# Revit family: IMH_ARR_10
name_source: partatom
category: Mechanical Equipment
units: mm (PartAtom-declared; Revit-internal decimal feet)

## family parameters
Always vertical = No
Cut with Voids When Loaded = No
Part Type = Normal
Room Calculation Point = No
Round Connector Dimension = Use Radius
Shared = No
Work Plane-Based = No

## types (44) — shared parameters
0 = 0"
1" = 1"
1.5 = 1 1/2"
2" = 2"
2' = 24"
3" = 3"
4" = 4"
90 = 90.00°
BAD = No
BAD_CCW = No
BAD_CW = No
BAU = No
BAU_CCW = No
BAU_CW = No
BHD = No
BHD_CCW = No
BHD_CW = No
CCW = No
CW = Yes
DBD = No
DBD_CCW = No
DBD_CW = No
FIRST_CURVE = 0"
L_RAD = 18 5/32"
Manufacturer = Loren Cook Company
NO = No
ONE EIGTH = 1/8"
TAD = No
TAD_CCW = No
TAD_CW = No
TAU = No
TAU_CCW = No
TAU_CW = No
THD = Yes
THD_CCW = No
THD_CW = Yes
UBD = No
UBD_CCW = No
UBD_CW = No
URL = www.lorencook.com
ZERO = 0.00°

## per-type parameters (varying)
- 70_MHA_ARR_10: (B + 1/4") / 2=3 1/16"; (C/2)+2"=5 1/2"; (C/2)-.125"=3 3/8"; (N-A)/2=1 31/32"; -((B + 1/4") / 2)=-3 1/16"; -D=-14 1/4"; -D+.125"=-14 1/8"; -F=-21 1/16"; -R*.75=-11 5/32"; 2S=8 1/2"; 2T=2 3/8"; 91*AA=8 1/32"; A=6 5/8"; A+.25"=6 7/8"; A/2=3 5/16"; A/5=1 5/16"; AA=8 13/16"; B=5 7/8"; B+.25"=6 1/8"; B/2=2 15/16"; BB=8 3/8"; C=7"; C/2=3 1/2"; D=14 1/4"; E=9 11/16"; E-2"=7 11/16"; E/2=4 27/32"; F=21 1/16"; G=26 1/4"; H=24 3/16"; J=4"; K=9 3/16"; L=9 11/16"; M=8 5/16"; M*.9=7"; M-(A/5)=7"; M/2=4 5/32"; Model=MHA; N=10 9/16"; N-A=3 15/16"; P=9/16"; P/2=9/32"; Q=7 7/16"; R=14 7/8"; R*.75=-11 5/32"; S=4 1/4"; SECOND_CURVE=27/32"; T=1 3/16"; T+T+1"=3 3/8"; T/2=19/32"; THIRD_CURVE=1 3/32"; Type Comments=Industrial Material Handler Backward Inclined Flat Blade Belt Driven Single Width, Single Inlet Arrangement 10; U=6 3/16"; UNIT_SIZE=70; W=6"; X=10 1/8"; Y=9 1/4"; Z=13 3/8"
- 90_MHA_ARR_10: (B + 1/4") / 2=3 7/8"; (C/2)+2"=6 1/2"; (C/2)-.125"=4 3/8"; (N-A)/2=2 17/32"; -((B + 1/4") / 2)=-3 7/8"; -D=-15 1/4"; -D+.125"=-15 1/8"; -F=-21 7/8"; -R*.75=-11 5/32"; 2S=10 1/8"; 2T=2 7/8"; 91*AA=10 3/16"; A=8 7/16"; A+.25"=8 11/16"; A/2=4 7/32"; A/5=1 11/16"; AA=11 3/16"; B=7 1/2"; B+.25"=7 3/4"; B/2=3 3/4"; BB=10 5/8"; C=9"; C/2=4 1/2"; D=15 1/4"; E=9 11/16"; E-2"=7 11/16"; E/2=4 27/32"; F=21 7/8"; G=27 7/8"; H=28 3/4"; J=4"; K=9 3/16"; L=12 5/16"; M=10 5/8"; M*.9=8 15/16"; M-(A/5)=8 15/16"; M/2=5 5/16"; Model=MHA; N=13 1/2"; N-A=5 1/16"; P=9/16"; P/2=9/32"; Q=7 7/16"; R=14 7/8"; R*.75=-11 5/32"; S=5 1/16"; SECOND_CURVE=1 1/16"; T=1 7/16"; T+T+1"=3 7/8"; T/2=23/32"; THIRD_CURVE=1 13/32"; Type Comments=Industrial Material Handler Backward Inclined Flat Blade Belt Driven Single Width, Single Inlet Arrangement 10; U=7"; UNIT_SIZE=90; W=6"; X=12 15/16"; Y=11 3/4"; Z=17 1/16"
- 110_MHA_ARR_10: (B + 1/4") / 2=4 11/16"; (C/2)+2"=7 1/2"; (C/2)-.125"=5 3/8"; (N-A)/2=3 1/32"; -((B + 1/4") / 2)=-4 11/16"; -D=-18 3/4"; -D+.125"=-18 5/8"; -F=-25"; -R*.75=-12 3/8"; 2S=13"; 2T=2 7/8"; 91*AA=12 1/2"; A=10 3/8"; A+.25"=10 5/8"; A/2=5 3/16"; A/5=2 1/16"; AA=13 3/4"; B=9 1/8"; B+.25"=9 3/8"; B/2=4 9/16"; BB=13 1/16"; C=11"; C/2=5 1/2"; D=18 3/4"; E=9 11/16"; E-2"=7 11/16"; E/2=4 27/32"; F=25"; G=32 7/8"; H=35 3/16"; J=4"; K=9 3/16"; L=15 1/16"; M=13"; M*.9=10 15/16"; M-(A/5)=10 15/16"; M/2=6 1/2"; Model=MHA; N=16 7/16"; N-A=6 1/16"; P=9/16"; P/2=9/32"; Q=8 1/4"; R=16 1/2"; R*.75=-12 3/8"; S=6 1/2"; SECOND_CURVE=1 5/16"; T=1 7/16"; T+T+1"=3 7/8"; T/2=23/32"; THIRD_CURVE=1 23/32"; Type Comments=Industrial Material Handler Backward Inclined Flat Blade Belt Driven Single Width, Single Inlet Arrangement 10; U=8 13/16"; UNIT_SIZE=110; W=8"; X=15 3/4"; Y=14 7/16"; Z=20 13/16"
- 130_MHA_ARR_10: (B + 1/4") / 2=5 9/16"; (C/2)+2"=8 1/2"; (C/2)-.125"=6 3/8"; (N-A)/2=3 5/8"; -((B + 1/4") / 2)=-5 9/16"; -D=-21 3/4"; -D+.125"=-21 5/8"; -F=-26 3/16"; -R*.75=-12 9/16"; 2S=14 3/4"; 2T=3 3/8"; 91*AA=14 23/32"; A=12 3/16"; A+.25"=12 7/16"; A/2=6 3/32"; A/5=2 7/16"; AA=16 3/16"; B=10 7/8"; B+.25"=11 1/8"; B/2=5 7/16"; BB=15 3/8"; C=13"; C/2=6 1/2"; D=21 3/4"; E=11 3/4"; E-2"=9 3/4"; E/2=5 7/8"; F=26 3/16"; G=34 7/8"; H=41 3/16"; J=5"; K=11"; L=17 13/16"; M=15 3/8"; M*.9=12 15/16"; M-(A/5)=12 15/16"; M/2=7 11/16"; Model=MHA; N=19 7/16"; N-A=7 1/4"; P=11/16"; P/2=11/32"; Q=8 3/8"; R=16 3/4"; R*.75=-12 9/16"; S=7 3/8"; SECOND_CURVE=1 17/32"; T=1 11/16"; T+T+1"=4 3/8"; T/2=27/32"; THIRD_CURVE=2 1/32"; Type Comments=Industrial Material Handler Backward Inclined Flat Blade Belt Driven Single Width, Single Inlet Arrangement 10; U=9 13/16"; UNIT_SIZE=130; W=8"; X=18 5/8"; Y=17"; Z=24 5/8"
- 150_MHA_ARR_10: (B + 1/4") / 2=6 13/32"; (C/2)+2"=9 1/2"; (C/2)-.125"=7 3/8"; (N-A)/2=4 5/32"; -((B + 1/4") / 2)=-6 13/32"; -D=-25 1/4"; -D+.125"=-25 1/8"; -F=-31 3/4"; -R*.75=-16 1/8"; 2S=16 7/16"; 2T=3 7/8"; 91*AA=17 3/16"; A=14 1/16"; A+.25"=14 5/16"; A/2=7 1/32"; A/5=2 13/16"; AA=18 7/8"; B=12 9/16"; B+.25"=12 13/16"; B/2=6 9/32"; BB=18"; C=15"; C/2=7 1/2"; D=25 1/4"; E=13"; E-2"=11"; E/2=6 1/2"; F=31 3/4"; G=41 5/16"; H=47 5/8"; J=5"; K=12 1/4"; L=20 5/8"; M=17 3/4"; M*.9=14 15/16"; M-(A/5)=14 15/16"; M/2=8 7/8"; Model=MHA; N=22 3/8"; N-A=8 5/16"; P=11/16"; P/2=11/32"; Q=10 3/4"; R=21 1/2"; R*.75=-16 1/8"; S=8 7/32"; SECOND_CURVE=1 3/4"; T=1 15/16"; T+T+1"=4 7/8"; T/2=31/32"; THIRD_CURVE=2 11/32"; Type Comments=Industrial Material Handler Backward Inclined Flat Blade Belt Driven Single Width, Single Inlet Arrangement 10; U=10 11/16"; UNIT_SIZE=150; W=8"; X=21 1/2"; Y=19 3/4"; Z=28 3/8"
- 170_MHA_ARR_10: (B + 1/4") / 2=7 1/4"; (C/2)+2"=10 1/2"; (C/2)-.125"=8 3/8"; (N-A)/2=4 11/16"; -((B + 1/4") / 2)=-7 1/4"; -D=-28 1/4"; -D+.125"=-28 1/8"; -F=-32 9/16"; -R*.75=-16 1/8"; 2S=18 1/8"; 2T=4 3/8"; 91*AA=19 11/32"; A=16"; A+.25"=16 1/4"; A/2=8"; A/5=3 3/16"; AA=21 1/4"; B=14 1/4"; B+.25"=14 1/2"; B/2=7 1/8"; BB=20 1/4"; C=17"; C/2=8 1/2"; D=28 1/4"; E=13 7/8"; E-2"=11 7/8"; E/2=6 15/16"; F=32 9/16"; G=43"; H=53 5/8"; J=6"; K=13 1/8"; L=23 3/4"; M=20 1/8"; M*.9=16 15/16"; M-(A/5)=16 15/16"; M/2=10 1/16"; Model=MHA; N=25 3/8"; N-A=9 3/8"; P=11/16"; P/2=11/32"; Q=10 3/4"; R=21 1/2"; R*.75=-16 1/8"; S=9 1/16"; SECOND_CURVE=2"; T=2 3/16"; T+T+1"=5 3/8"; T/2=1 3/32"; THIRD_CURVE=2 21/32"; Type Comments=Industrial Material Handler Backward Inclined Flat Blade Belt Driven Single Width, Single Inlet Arrangement 10; U=11 1/2"; UNIT_SIZE=170; W=8"; X=24 9/16"; Y=22 1/2"; Z=32 3/16"
- 190_MHA_ARR_10: (B + 1/4") / 2=8 1/16"; (C/2)+2"=11 1/2"; (C/2)-.125"=9 3/8"; (N-A)/2=5 7/32"; -((B + 1/4") / 2)=-8 1/16"; -D=-31 1/4"; -D+.125"=-31 1/8"; -F=-34 11/16"; -R*.75=-17 1/16"; 2S=19 7/8"; 2T=4 7/8"; 91*AA=21 5/8"; A=17 13/16"; A+.25"=18 1/16"; A/2=8 29/32"; A/5=3 9/16"; AA=23 3/4"; B=15 7/8"; B+.25"=16 1/8"; B/2=7 15/16"; BB=22 5/8"; C=19"; C/2=9 1/2"; D=31 1/4"; E=15 5/16"; E-2"=13 5/16"; E/2=7 21/32"; F=34 11/16"; G=46"; H=59 1/2"; J=6"; K=14 9/16"; L=25 15/16"; M=22 7/16"; M*.9=18 7/8"; M-(A/5)=18 7/8"; M/2=11 7/32"; Model=MHA; N=28 1/4"; N-A=10 7/16"; P=11/16"; P/2=11/32"; Q=11 3/8"; R=22 3/4"; R*.75=-17 1/16"; S=9 15/16"; SECOND_CURVE=2 7/32"; T=2 7/16"; T+T+1"=5 7/8"; T/2=1 7/32"; THIRD_CURVE=2 31/32"; Type Comments=Industrial Material Handler Backward Inclined Flat Blade Belt Driven Single Width, Single Inlet Arrangement 10; U=12 5/16"; UNIT_SIZE=190; W=8"; X=27 1/8"; Y=24 7/8"; Z=35 13/16"
- 210_MHA_ARR_10: (B + 1/4") / 2=8 29/32"; (C/2)+2"=12 1/2"; (C/2)-.125"=10 3/8"; (N-A)/2=5 3/4"; -((B + 1/4") / 2)=-8 29/32"; -D=-34 1/2"; -D+.125"=-34 3/8"; -F=-38 1/4"; -R*.75=-19 1/8"; 2S=21 5/16"; 2T=4 7/8"; 91*AA=23 7/16"; A=19 3/4"; A+.25"=20"; A/2=9 7/8"; A/5=3 15/16"; AA=25 3/4"; B=17 9/16"; B+.25"=17 13/16"; B/2=8 25/32"; BB=24 3/8"; C=21"; C/2=10 1/2"; D=34 1/2"; E=16 9/16"; E-2"=14 9/16"; E/2=8 9/32"; F=38 1/4"; G=50 3/8"; H=65 3/4"; J=6"; K=15 13/16"; L=28 1/2"; M=23"; M*.9=19 1/16"; M-(A/5)=19 1/16"; M/2=11 1/2"; Model=MHA; N=31 1/4"; N-A=11 1/2"; P=11/16"; P/2=11/32"; Q=12 3/4"; R=25 1/2"; R*.75=-19 1/8"; S=10 21/32"; SECOND_CURVE=2 15/32"; T=2 7/16"; T+T+1"=5 7/8"; T/2=1 7/32"; THIRD_CURVE=3 9/32"; Type Comments=Industrial Material Handler Backward Inclined Flat Blade Belt Driven Single Width, Single Inlet Arrangement 10; U=13 3/16"; UNIT_SIZE=210; W=8"; X=29 7/8"; Y=27 1/8"; Z=38 3/8"
- 230_MHA_ARR_10: (B + 1/4") / 2=9 3/4"; (C/2)+2"=13 1/2"; (C/2)-.125"=11 3/8"; (N-A)/2=6 11/32"; -((B + 1/4") / 2)=-9 3/4"; -D=-37 1/2"; -D+.125"=-37 3/8"; -F=-41 1/8"; -R*.75=-20 5/32"; 2S=24 5/8"; 2T=5 3/8"; 91*AA=25 3/4"; A=21 5/8"; A+.25"=21 7/8"; A/2=10 13/16"; A/5=4 5/16"; AA=28 5/16"; B=19 1/4"; B+.25"=19 1/2"; B/2=9 5/8"; BB=26 13/16"; C=23"; C/2=11 1/2"; D=37 1/2"; E=18 13/16"; E-2"=16 13/16"; E/2=9 13/32"; F=41 1/8"; G=55 1/4"; H=71 13/16"; J=7"; K=17 9/16"; L=31 1/4"; M=26"; M*.9=21 11/16"; M-(A/5)=21 11/16"; M/2=13"; Model=MHA; N=34 5/16"; N-A=12 11/16"; P=13/16"; P/2=13/32"; Q=13 7/16"; R=26 7/8"; R*.75=-20 5/32"; S=12 5/16"; SECOND_CURVE=2 23/32"; T=2 11/16"; T+T+1"=6 3/8"; T/2=1 11/32"; THIRD_CURVE=3 19/32"; Type Comments=Industrial Material Handler Backward Inclined Flat Blade Belt Driven Single Width, Single Inlet Arrangement 10; U=15 1/8"; UNIT_SIZE=230; W=8"; X=32 13/16"; Y=29 13/16"; Z=42 5/8"
- 260_MHA_ARR_10: (B + 1/4") / 2=11"; (C/2)+2"=15"; (C/2)-.125"=12 7/8"; (N-A)/2=8 3/8"; -((B + 1/4") / 2)=-11"; -D=-41 3/4"; -D+.125"=-41 5/8"; -F=-43 15/16"; -R*.75=-20 13/16"; 2S=27 1/8"; 2T=5 3/8"; 91*AA=29"; A=24 7/16"; A+.25"=24 11/16"; A/2=12 7/32"; A/5=4 7/8"; AA=31 7/8"; B=21 3/4"; B+.25"=22"; B/2=10 7/8"; BB=30 1/4"; C=26"; C/2=13"; D=41 3/4"; E=20 5/8"; E-2"=18 5/8"; E/2=10 5/16"; F=43 15/16"; G=58 11/16"; H=82 15/16"; J=7"; K=19 3/8"; L=35 1/8"; M=29"; M*.9=24 1/8"; M-(A/5)=24 1/8"; M/2=14 1/2"; Model=MHA; N=41 3/16"; N-A=16 3/4"; P=13/16"; P/2=13/32"; Q=13 7/8"; R=27 3/4"; R*.75=-20 13/16"; S=13 9/16"; SECOND_CURVE=3 1/16"; T=2 11/16"; T+T+1"=6 3/8"; T/2=1 11/32"; THIRD_CURVE=4 1/16"; Type Comments=Industrial Material Handler Backward Inclined Flat Blade Belt Driven Single Width, Single Inlet Arrangement 10; U=16 3/8"; UNIT_SIZE=260; W=8"; X=38 3/16"; Y=33 1/2"; Z=49 5/8"
- 290_MHA_ARR_10: (B + 1/4") / 2=12 1/4"; (C/2)+2"=16 1/2"; (C/2)-.125"=14 3/8"; (N-A)/2=9 9/32"; -((B + 1/4") / 2)=-12 1/4"; -D=-46 1/2"; -D+.125"=-46 3/8"; -F=-45 9/16"; -R*.75=-21 9/16"; 2S=29 5/8"; 2T=5 7/8"; 91*AA=32 17/32"; A=27 5/16"; A+.25"=27 9/16"; A/2=13 21/32"; A/5=5 15/32"; AA=35 3/4"; B=24 1/4"; B+.25"=24 1/2"; B/2=12 1/8"; BB=33 7/8"; C=29"; C/2=14 1/2"; D=46 1/2"; E=22 1/2"; E-2"=20 1/2"; E/2=11 1/4"; F=45 9/16"; G=62 3/16"; H=92 1/2"; J=8"; K=21 1/4"; L=39 1/2"; M=31 3/4"; M*.9=26 9/32"; M-(A/5)=26 9/32"; M/2=15 7/8"; Model=MHA; N=45 7/8"; N-A=18 9/16"; P=13/16"; P/2=13/32"; Q=14 3/8"; R=28 3/4"; R*.75=-21 9/16"; S=14 13/16"; SECOND_CURVE=3 13/32"; T=2 15/16"; T+T+1"=6 7/8"; T/2=1 15/32"; THIRD_CURVE=4 9/16"; Type Comments=Industrial Material Handler Backward Inclined Flat Blade Belt Driven Single Width, Single Inlet Arrangement 10; U=17 5/8"; UNIT_SIZE=290; W=8"; X=42 11/16"; Y=37 5/8"; Z=54 7/8"
- 110_MHB_ARR_10: (B + 1/4") / 2=4 11/16"; (C/2)+2"=7 1/2"; (C/2)-.125"=5 3/8"; (N-A)/2=3 1/32"; -((B + 1/4") / 2)=-4 11/16"; -D=-18 3/4"; -D+.125"=-18 5/8"; -F=-25"; -R*.75=-12 3/8"; 2S=13"; 2T=2 7/8"; 91*AA=12 1/2"; A=10 3/8"; A+.25"=10 5/8"; A/2=5 3/16"; A/5=2 1/16"; AA=13 3/4"; B=9 1/8"; B+.25"=9 3/8"; B/2=4 9/16"; BB=13 1/16"; C=11"; C/2=5 1/2"; D=18 3/4"; E=9 11/16"; E-2"=7 11/16"; E/2=4 27/32"; F=25"; G=32 7/8"; H=35 3/16"; J=4"; K=9 3/16"; L=15 1/16"; M=13"; M*.9=10 15/16"; M-(A/5)=10 15/16"; M/2=6 1/2"; Model=MHB; N=16 7/16"; N-A=6 1/16"; P=9/16"; P/2=9/32"; Q=8 1/4"; R=16 1/2"; R*.75=-12 3/8"; S=6 1/2"; SECOND_CURVE=1 5/16"; T=1 7/16"; T+T+1"=3 7/8"; T/2=23/32"; THIRD_CURVE=1 23/32"; Type Comments=Industrial Material Handler Backward Inclined Backplated Radial Blade Belt Driven Single Width, Single Inlet Arrangement 10; U=8 13/16"; UNIT_SIZE=110; W=8"; X=15 3/4"; Y=14 7/16"; Z=20 13/16"
- 110_MHR_ARR_10: (B + 1/4") / 2=4 11/16"; (C/2)+2"=7 1/2"; (C/2)-.125"=5 3/8"; (N-A)/2=3 1/32"; -((B + 1/4") / 2)=-4 11/16"; -D=-18 3/4"; -D+.125"=-18 5/8"; -F=-25"; -R*.75=-12 3/8"; 2S=13"; 2T=2 7/8"; 91*AA=12 1/2"; A=10 3/8"; A+.25"=10 5/8"; A/2=5 3/16"; A/5=2 1/16"; AA=13 3/4"; B=9 1/8"; B+.25"=9 3/8"; B/2=4 9/16"; BB=13 1/16"; C=11"; C/2=5 1/2"; D=18 3/4"; E=9 11/16"; E-2"=7 11/16"; E/2=4 27/32"; F=25"; G=32 7/8"; H=35 3/16"; J=4"; K=9 3/16"; L=15 1/16"; M=13"; M*.9=10 15/16"; M-(A/5)=10 15/16"; M/2=6 1/2"; Model=MHR; N=16 7/16"; N-A=6 1/16"; P=9/16"; P/2=9/32"; Q=8 1/4"; R=16 1/2"; R*.75=-12 3/8"; S=6 1/2"; SECOND_CURVE=1 5/16"; T=1 7/16"; T+T+1"=3 7/8"; T/2=23/32"; THIRD_CURVE=1 23/32"; Type Comments=Industrial Material Handler Backward Inclined Reinforced Radial Blade Belt Driven Single Width, Single Inlet Arrangement 10; U=8 13/16"; UNIT_SIZE=110; W=8"; X=15 3/4"; Y=14 7/16"; Z=20 13/16"
- 130_MHB_ARR_10: (B + 1/4") / 2=5 9/16"; (C/2)+2"=8 1/2"; (C/2)-.125"=6 3/8"; (N-A)/2=3 5/8"; -((B + 1/4") / 2)=-5 9/16"; -D=-21 3/4"; -D+.125"=-21 5/8"; -F=-26 3/16"; -R*.75=-12 9/16"; 2S=14 3/4"; 2T=3 3/8"; 91*AA=14 23/32"; A=12 3/16"; A+.25"=12 7/16"; A/2=6 3/32"; A/5=2 7/16"; AA=16 3/16"; B=10 7/8"; B+.25"=11 1/8"; B/2=5 7/16"; BB=15 3/8"; C=13"; C/2=6 1/2"; D=21 3/4"; E=11 3/4"; E-2"=9 3/4"; E/2=5 7/8"; F=26 3/16"; G=34 7/8"; H=41 3/16"; J=5"; K=11"; L=17 13/16"; M=15 3/8"; M*.9=12 15/16"; M-(A/5)=12 15/16"; M/2=7 11/16"; Model=MHB; N=19 7/16"; N-A=7 1/4"; P=11/16"; P/2=11/32"; Q=8 3/8"; R=16 3/4"; R*.75=-12 9/16"; S=7 3/8"; SECOND_CURVE=1 17/32"; T=1 11/16"; T+T+1"=4 3/8"; T/2=27/32"; THIRD_CURVE=2 1/32"; Type Comments=Industrial Material Handler Backward Inclined Backplated Radial Blade Belt Driven Single Width, Single Inlet Arrangement 10; U=9 13/16"; UNIT_SIZE=130; W=8"; X=18 5/8"; Y=17"; Z=24 5/8"
- 130_MHR_ARR_10: (B + 1/4") / 2=5 9/16"; (C/2)+2"=8 1/2"; (C/2)-.125"=6 3/8"; (N-A)/2=3 5/8"; -((B + 1/4") / 2)=-5 9/16"; -D=-21 3/4"; -D+.125"=-21 5/8"; -F=-26 3/16"; -R*.75=-12 9/16"; 2S=14 3/4"; 2T=3 3/8"; 91*AA=14 23/32"; A=12 3/16"; A+.25"=12 7/16"; A/2=6 3/32"; A/5=2 7/16"; AA=16 3/16"; B=10 7/8"; B+.25"=11 1/8"; B/2=5 7/16"; BB=15 3/8"; C=13"; C/2=6 1/2"; D=21 3/4"; E=11 3/4"; E-2"=9 3/4"; E/2=5 7/8"; F=26 3/16"; G=34 7/8"; H=41 3/16"; J=5"; K=11"; L=17 13/16"; M=15 3/8"; M*.9=12 15/16"; M-(A/5)=12 15/16"; M/2=7 11/16"; Model=MHR; N=19 7/16"; N-A=7 1/4"; P=11/16"; P/2=11/32"; Q=8 3/8"; R=16 3/4"; R*.75=-12 9/16"; S=7 3/8"; SECOND_CURVE=1 17/32"; T=1 11/16"; T+T+1"=4 3/8"; T/2=27/32"; THIRD_CURVE=2 1/32"; Type Comments=Industrial Material Handler Backward Inclined Reinforced Radial Blade Belt Driven Single Width, Single Inlet Arrangement 10; U=9 13/16"; UNIT_SIZE=130; W=8"; X=18 5/8"; Y=17"; Z=24 5/8"
- 150_MHB_ARR_10: (B + 1/4") / 2=6 13/32"; (C/2)+2"=9 1/2"; (C/2)-.125"=7 3/8"; (N-A)/2=4 5/32"; -((B + 1/4") / 2)=-6 13/32"; -D=-25 1/4"; -D+.125"=-25 1/8"; -F=-31 3/4"; -R*.75=-16 1/8"; 2S=16 7/16"; 2T=3 7/8"; 91*AA=17 3/16"; A=14 1/16"; A+.25"=14 5/16"; A/2=7 1/32"; A/5=2 13/16"; AA=18 7/8"; B=12 9/16"; B+.25"=12 13/16"; B/2=6 9/32"; BB=18"; C=15"; C/2=7 1/2"; D=25 1/4"; E=13"; E-2"=11"; E/2=6 1/2"; F=31 3/4"; G=41 5/16"; H=47 5/8"; J=5"; K=12 1/4"; L=20 5/8"; M=17 3/4"; M*.9=14 15/16"; M-(A/5)=14 15/16"; M/2=8 7/8"; Model=MHB; N=22 3/8"; N-A=8 5/16"; P=11/16"; P/2=11/32"; Q=10 3/4"; R=21 1/2"; R*.75=-16 1/8"; S=8 7/32"; SECOND_CURVE=1 3/4"; T=1 15/16"; T+T+1"=4 7/8"; T/2=31/32"; THIRD_CURVE=2 11/32"; Type Comments=Industrial Material Handler Backward Inclined Backplated Radial Blade Belt Driven Single Width, Single Inlet Arrangement 10; U=10 11/16"; UNIT_SIZE=150; W=8"; X=21 1/2"; Y=19 3/4"; Z=28 3/8"
- 150_MHR_ARR_10: (B + 1/4") / 2=6 13/32"; (C/2)+2"=9 1/2"; (C/2)-.125"=7 3/8"; (N-A)/2=4 5/32"; -((B + 1/4") / 2)=-6 13/32"; -D=-25 1/4"; -D+.125"=-25 1/8"; -F=-31 3/4"; -R*.75=-16 1/8"; 2S=16 7/16"; 2T=3 7/8"; 91*AA=17 3/16"; A=14 1/16"; A+.25"=14 5/16"; A/2=7 1/32"; A/5=2 13/16"; AA=18 7/8"; B=12 9/16"; B+.25"=12 13/16"; B/2=6 9/32"; BB=18"; C=15"; C/2=7 1/2"; D=25 1/4"; E=13"; E-2"=11"; E/2=6 1/2"; F=31 3/4"; G=41 5/16"; H=47 5/8"; J=5"; K=12 1/4"; L=20 5/8"; M=17 3/4"; M*.9=14 15/16"; M-(A/5)=14 15/16"; M/2=8 7/8"; Model=MHR; N=22 3/8"; N-A=8 5/16"; P=11/16"; P/2=11/32"; Q=10 3/4"; R=21 1/2"; R*.75=-16 1/8"; S=8 7/32"; SECOND_CURVE=1 3/4"; T=1 15/16"; T+T+1"=4 7/8"; T/2=31/32"; THIRD_CURVE=2 11/32"; Type Comments=Industrial Material Handler Backward Inclined Reinforced Radial Blade Belt Driven Single Width, Single Inlet Arrangement 10; U=10 11/16"; UNIT_SIZE=150; W=8"; X=21 1/2"; Y=19 3/4"; Z=28 3/8"
- 170_MHB_ARR_10: (B + 1/4") / 2=7 1/4"; (C/2)+2"=10 1/2"; (C/2)-.125"=8 3/8"; (N-A)/2=4 11/16"; -((B + 1/4") / 2)=-7 1/4"; -D=-28 1/4"; -D+.125"=-28 1/8"; -F=-32 9/16"; -R*.75=-16 1/8"; 2S=18 1/8"; 2T=4 3/8"; 91*AA=19 11/32"; A=16"; A+.25"=16 1/4"; A/2=8"; A/5=3 3/16"; AA=21 1/4"; B=14 1/4"; B+.25"=14 1/2"; B/2=7 1/8"; BB=20 1/4"; C=17"; C/2=8 1/2"; D=28 1/4"; E=13 7/8"; E-2"=11 7/8"; E/2=6 15/16"; F=32 9/16"; G=43"; H=53 5/8"; J=6"; K=13 1/8"; L=23 3/4"; M=20 1/8"; M*.9=16 15/16"; M-(A/5)=16 15/16"; M/2=10 1/16"; Model=MHB; N=25 3/8"; N-A=9 3/8"; P=11/16"; P/2=11/32"; Q=10 3/4"; R=21 1/2"; R*.75=-16 1/8"; S=9 1/16"; SECOND_CURVE=2"; T=2 3/16"; T+T+1"=5 3/8"; T/2=1 3/32"; THIRD_CURVE=2 21/32"; Type Comments=Industrial Material Handler Backward Inclined Backplated Radial Blade Belt Driven Single Width, Single Inlet Arrangement 10; U=11 1/2"; UNIT_SIZE=170; W=8"; X=24 9/16"; Y=22 1/2"; Z=32 3/16"
- 170_MHR_ARR_10: (B + 1/4") / 2=7 1/4"; (C/2)+2"=10 1/2"; (C/2)-.125"=8 3/8"; (N-A)/2=4 11/16"; -((B + 1/4") / 2)=-7 1/4"; -D=-28 1/4"; -D+.125"=-28 1/8"; -F=-32 9/16"; -R*.75=-16 1/8"; 2S=18 1/8"; 2T=4 3/8"; 91*AA=19 11/32"; A=16"; A+.25"=16 1/4"; A/2=8"; A/5=3 3/16"; AA=21 1/4"; B=14 1/4"; B+.25"=14 1/2"; B/2=7 1/8"; BB=20 1/4"; C=17"; C/2=8 1/2"; D=28 1/4"; E=13 7/8"; E-2"=11 7/8"; E/2=6 15/16"; F=32 9/16"; G=43"; H=53 5/8"; J=6"; K=13 1/8"; L=23 3/4"; M=20 1/8"; M*.9=16 15/16"; M-(A/5)=16 15/16"; M/2=10 1/16"; Model=MHR; N=25 3/8"; N-A=9 3/8"; P=11/16"; P/2=11/32"; Q=10 3/4"; R=21 1/2"; R*.75=-16 1/8"; S=9 1/16"; SECOND_CURVE=2"; T=2 3/16"; T+T+1"=5 3/8"; T/2=1 3/32"; THIRD_CURVE=2 21/32"; Type Comments=Industrial Material Handler Backward Inclined Reinforced Radial Blade Belt Driven Single Width, Single Inlet Arrangement 10; U=11 1/2"; UNIT_SIZE=170; W=8"; X=24 9/16"; Y=22 1/2"; Z=32 3/16"
- 190_MHB_ARR_10: (B + 1/4") / 2=8 1/16"; (C/2)+2"=11 1/2"; (C/2)-.125"=9 3/8"; (N-A)/2=5 7/32"; -((B + 1/4") / 2)=-8 1/16"; -D=-31 1/4"; -D+.125"=-31 1/8"; -F=-34 11/16"; -R*.75=-17 1/16"; 2S=19 7/8"; 2T=4 7/8"; 91*AA=21 5/8"; A=17 13/16"; A+.25"=18 1/16"; A/2=8 29/32"; A/5=3 9/16"; AA=23 3/4"; B=15 7/8"; B+.25"=16 1/8"; B/2=7 15/16"; BB=22 5/8"; C=19"; C/2=9 1/2"; D=31 1/4"; E=15 5/16"; E-2"=13 5/16"; E/2=7 21/32"; F=34 11/16"; G=46"; H=59 1/2"; J=6"; K=14 9/16"; L=25 15/16"; M=22 7/16"; M*.9=18 7/8"; M-(A/5)=18 7/8"; M/2=11 7/32"; Model=MHB; N=28 1/4"; N-A=10 7/16"; P=11/16"; P/2=11/32"; Q=11 3/8"; R=22 3/4"; R*.75=-17 1/16"; S=9 15/16"; SECOND_CURVE=2 7/32"; T=2 7/16"; T+T+1"=5 7/8"; T/2=1 7/32"; THIRD_CURVE=2 31/32"; Type Comments=Industrial Material Handler Backward Inclined Backplated Radial Blade Belt Driven Single Width, Single Inlet Arrangement 10; U=12 5/16"; UNIT_SIZE=190; W=8"; X=27 1/8"; Y=24 7/8"; Z=35 13/16"
- 190_MHR_ARR_10: (B + 1/4") / 2=8 1/16"; (C/2)+2"=11 1/2"; (C/2)-.125"=9 3/8"; (N-A)/2=5 7/32"; -((B + 1/4") / 2)=-8 1/16"; -D=-31 1/4"; -D+.125"=-31 1/8"; -F=-34 11/16"; -R*.75=-17 1/16"; 2S=19 7/8"; 2T=4 7/8"; 91*AA=21 5/8"; A=17 13/16"; A+.25"=18 1/16"; A/2=8 29/32"; A/5=3 9/16"; AA=23 3/4"; B=15 7/8"; B+.25"=16 1/8"; B/2=7 15/16"; BB=22 5/8"; C=19"; C/2=9 1/2"; D=31 1/4"; E=15 5/16"; E-2"=13 5/16"; E/2=7 21/32"; F=34 11/16"; G=46"; H=59 1/2"; J=6"; K=14 9/16"; L=25 15/16"; M=22 7/16"; M*.9=18 7/8"; M-(A/5)=18 7/8"; M/2=11 7/32"; Model=MHR; N=28 1/4"; N-A=10 7/16"; P=11/16"; P/2=11/32"; Q=11 3/8"; R=22 3/4"; R*.75=-17 1/16"; S=9 15/16"; SECOND_CURVE=2 7/32"; T=2 7/16"; T+T+1"=5 7/8"; T/2=1 7/32"; THIRD_CURVE=2 31/32"; Type Comments=Industrial Material Handler Backward Inclined Reinforced Radial Blade Belt Driven Single Width, Single Inlet Arrangement 10; U=12 5/16"; UNIT_SIZE=190; W=8"; X=27 1/8"; Y=24 7/8"; Z=35 13/16"
- 210_MHB_ARR_10: (B + 1/4") / 2=8 29/32"; (C/2)+2"=12 1/2"; (C/2)-.125"=10 3/8"; (N-A)/2=5 3/4"; -((B + 1/4") / 2)=-8 29/32"; -D=-34 1/2"; -D+.125"=-34 3/8"; -F=-38 1/4"; -R*.75=-19 1/8"; 2S=21 5/16"; 2T=4 7/8"; 91*AA=23 7/16"; A=19 3/4"; A+.25"=20"; A/2=9 7/8"; A/5=3 15/16"; AA=25 3/4"; B=17 9/16"; B+.25"=17 13/16"; B/2=8 25/32"; BB=24 3/8"; C=21"; C/2=10 1/2"; D=34 1/2"; E=16 9/16"; E-2"=14 9/16"; E/2=8 9/32"; F=38 1/4"; G=50 3/8"; H=65 3/4"; J=6"; K=15 13/16"; L=28 1/2"; M=23"; M*.9=19 1/16"; M-(A/5)=19 1/16"; M/2=11 1/2"; Model=MHB; N=31 1/4"; N-A=11 1/2"; P=11/16"; P/2=11/32"; Q=12 3/4"; R=25 1/2"; R*.75=-19 1/8"; S=10 21/32"; SECOND_CURVE=2 15/32"; T=2 7/16"; T+T+1"=5 7/8"; T/2=1 7/32"; THIRD_CURVE=3 9/32"; Type Comments=Industrial Material Handler Backward Inclined Backplated Radial Blade Belt Driven Single Width, Single Inlet Arrangement 10; U=13 3/16"; UNIT_SIZE=210; W=8"; X=29 7/8"; Y=27 1/8"; Z=38 3/8"
- 210_MHR_ARR_10: (B + 1/4") / 2=8 29/32"; (C/2)+2"=12 1/2"; (C/2)-.125"=10 3/8"; (N-A)/2=5 3/4"; -((B + 1/4") / 2)=-8 29/32"; -D=-34 1/2"; -D+.125"=-34 3/8"; -F=-38 1/4"; -R*.75=-19 1/8"; 2S=21 5/16"; 2T=4 7/8"; 91*AA=23 7/16"; A=19 3/4"; A+.25"=20"; A/2=9 7/8"; A/5=3 15/16"; AA=25 3/4"; B=17 9/16"; B+.25"=17 13/16"; B/2=8 25/32"; BB=24 3/8"; C=21"; C/2=10 1/2"; D=34 1/2"; E=16 9/16"; E-2"=14 9/16"; E/2=8 9/32"; F=38 1/4"; G=50 3/8"; H=65 3/4"; J=6"; K=15 13/16"; L=28 1/2"; M=23"; M*.9=19 1/16"; M-(A/5)=19 1/16"; M/2=11 1/2"; Model=MHR; N=31 1/4"; N-A=11 1/2"; P=11/16"; P/2=11/32"; Q=12 3/4"; R=25 1/2"; R*.75=-19 1/8"; S=10 21/32"; SECOND_CURVE=2 15/32"; T=2 7/16"; T+T+1"=5 7/8"; T/2=1 7/32"; THIRD_CURVE=3 9/32"; Type Comments=Industrial Material Handler Backward Inclined Reinforced Radial Blade Belt Driven Single Width, Single Inlet Arrangement 10; U=13 3/16"; UNIT_SIZE=210; W=8"; X=29 7/8"; Y=27 1/8"; Z=38 3/8"
- 230_MHB_ARR_10: (B + 1/4") / 2=9 3/4"; (C/2)+2"=13 1/2"; (C/2)-.125"=11 3/8"; (N-A)/2=6 11/32"; -((B + 1/4") / 2)=-9 3/4"; -D=-37 1/2"; -D+.125"=-37 3/8"; -F=-41 1/8"; -R*.75=-20 5/32"; 2S=24 5/8"; 2T=5 3/8"; 91*AA=25 3/4"; A=21 5/8"; A+.25"=21 7/8"; A/2=10 13/16"; A/5=4 5/16"; AA=28 5/16"; B=19 1/4"; B+.25"=19 1/2"; B/2=9 5/8"; BB=26 13/16"; C=23"; C/2=11 1/2"; D=37 1/2"; E=18 13/16"; E-2"=16 13/16"; E/2=9 13/32"; F=41 1/8"; G=55 1/4"; H=71 13/16"; J=7"; K=17 9/16"; L=31 1/4"; M=26"; M*.9=21 11/16"; M-(A/5)=21 11/16"; M/2=13"; Model=MHB; N=34 5/16"; N-A=12 11/16"; P=13/16"; P/2=13/32"; Q=13 7/16"; R=26 7/8"; R*.75=-20 5/32"; S=12 5/16"; SECOND_CURVE=2 23/32"; T=2 11/16"; T+T+1"=6 3/8"; T/2=1 11/32"; THIRD_CURVE=3 19/32"; Type Comments=Industrial Material Handler Backward Inclined Backplated Radial Blade Belt Driven Single Width, Single Inlet Arrangement 10; U=15 1/8"; UNIT_SIZE=230; W=8"; X=32 13/16"; Y=29 13/16"; Z=42 5/8"
- 230_MHR_ARR_10: (B + 1/4") / 2=9 3/4"; (C/2)+2"=13 1/2"; (C/2)-.125"=11 3/8"; (N-A)/2=6 11/32"; -((B + 1/4") / 2)=-9 3/4"; -D=-37 1/2"; -D+.125"=-37 3/8"; -F=-41 1/8"; -R*.75=-20 5/32"; 2S=24 5/8"; 2T=5 3/8"; 91*AA=25 3/4"; A=21 5/8"; A+.25"=21 7/8"; A/2=10 13/16"; A/5=4 5/16"; AA=28 5/16"; B=19 1/4"; B+.25"=19 1/2"; B/2=9 5/8"; BB=26 13/16"; C=23"; C/2=11 1/2"; D=37 1/2"; E=18 13/16"; E-2"=16 13/16"; E/2=9 13/32"; F=41 1/8"; G=55 1/4"; H=71 13/16"; J=7"; K=17 9/16"; L=31 1/4"; M=26"; M*.9=21 11/16"; M-(A/5)=21 11/16"; M/2=13"; Model=MHR; N=34 5/16"; N-A=12 11/16"; P=13/16"; P/2=13/32"; Q=13 7/16"; R=26 7/8"; R*.75=-20 5/32"; S=12 5/16"; SECOND_CURVE=2 23/32"; T=2 11/16"; T+T+1"=6 3/8"; T/2=1 11/32"; THIRD_CURVE=3 19/32"; Type Comments=Industrial Material Handler Backward Inclined Reinforced Radial Blade Belt Driven Single Width, Single Inlet Arrangement 10; U=15 1/8"; UNIT_SIZE=230; W=8"; X=32 13/16"; Y=29 13/16"; Z=42 5/8"
- 260_MHB_ARR_10: (B + 1/4") / 2=11"; (C/2)+2"=15"; (C/2)-.125"=12 7/8"; (N-A)/2=8 3/8"; -((B + 1/4") / 2)=-11"; -D=-41 3/4"; -D+.125"=-41 5/8"; -F=-43 15/16"; -R*.75=-20 13/16"; 2S=27 1/8"; 2T=5 3/8"; 91*AA=29"; A=24 7/16"; A+.25"=24 11/16"; A/2=12 7/32"; A/5=4 7/8"; AA=31 7/8"; B=21 3/4"; B+.25"=22"; B/2=10 7/8"; BB=30 1/4"; C=26"; C/2=13"; D=41 3/4"; E=20 5/8"; E-2"=18 5/8"; E/2=10 5/16"; F=43 15/16"; G=58 11/16"; H=82 15/16"; J=7"; K=19 3/8"; L=35 1/8"; M=29"; M*.9=24 1/8"; M-(A/5)=24 1/8"; M/2=14 1/2"; Model=MHB; N=41 3/16"; N-A=16 3/4"; P=13/16"; P/2=13/32"; Q=13 7/8"; R=27 3/4"; R*.75=-20 13/16"; S=13 9/16"; SECOND_CURVE=3 1/16"; T=2 11/16"; T+T+1"=6 3/8"; T/2=1 11/32"; THIRD_CURVE=4 1/16"; Type Comments=Industrial Material Handler Backward Inclined Backplated Radial Blade Belt Driven Single Width, Single Inlet Arrangement 10; U=16 3/8"; UNIT_SIZE=260; W=8"; X=38 3/16"; Y=33 1/2"; Z=49 5/8"
- 260_MHR_ARR_10: (B + 1/4") / 2=11"; (C/2)+2"=15"; (C/2)-.125"=12 7/8"; (N-A)/2=8 3/8"; -((B + 1/4") / 2)=-11"; -D=-41 3/4"; -D+.125"=-41 5/8"; -F=-43 15/16"; -R*.75=-20 13/16"; 2S=27 1/8"; 2T=5 3/8"; 91*AA=29"; A=24 7/16"; A+.25"=24 11/16"; A/2=12 7/32"; A/5=4 7/8"; AA=31 7/8"; B=21 3/4"; B+.25"=22"; B/2=10 7/8"; BB=30 1/4"; C=26"; C/2=13"; D=41 3/4"; E=20 5/8"; E-2"=18 5/8"; E/2=10 5/16"; F=43 15/16"; G=58 11/16"; H=82 15/16"; J=7"; K=19 3/8"; L=35 1/8"; M=29"; M*.9=24 1/8"; M-(A/5)=24 1/8"; M/2=14 1/2"; Model=MHR; N=41 3/16"; N-A=16 3/4"; P=13/16"; P/2=13/32"; Q=13 7/8"; R=27 3/4"; R*.75=-20 13/16"; S=13 9/16"; SECOND_CURVE=3 1/16"; T=2 11/16"; T+T+1"=6 3/8"; T/2=1 11/32"; THIRD_CURVE=4 1/16"; Type Comments=Industrial Material Handler Backward Inclined Reinforced Radial Blade Belt Driven Single Width, Single Inlet Arrangement 10; U=16 3/8"; UNIT_SIZE=260; W=8"; X=38 3/16"; Y=33 1/2"; Z=49 5/8"
- 290_MHB_ARR_10: (B + 1/4") / 2=12 1/4"; (C/2)+2"=16 1/2"; (C/2)-.125"=14 3/8"; (N-A)/2=9 9/32"; -((B + 1/4") / 2)=-12 1/4"; -D=-46 1/2"; -D+.125"=-46 3/8"; -F=-45 9/16"; -R*.75=-21 9/16"; 2S=29 5/8"; 2T=5 7/8"; 91*AA=32 17/32"; A=27 5/16"; A+.25"=27 9/16"; A/2=13 21/32"; A/5=5 15/32"; AA=35 3/4"; B=24 1/4"; B+.25"=24 1/2"; B/2=12 1/8"; BB=33 7/8"; C=29"; C/2=14 1/2"; D=46 1/2"; E=22 1/2"; E-2"=20 1/2"; E/2=11 1/4"; F=45 9/16"; G=62 3/16"; H=92 1/2"; J=8"; K=21 1/4"; L=39 1/2"; M=31 3/4"; M*.9=26 9/32"; M-(A/5)=26 9/32"; M/2=15 7/8"; Model=MHB; N=45 7/8"; N-A=18 9/16"; P=13/16"; P/2=13/32"; Q=14 3/8"; R=28 3/4"; R*.75=-21 9/16"; S=14 13/16"; SECOND_CURVE=3 13/32"; T=2 15/16"; T+T+1"=6 7/8"; T/2=1 15/32"; THIRD_CURVE=4 9/16"; Type Comments=Industrial Material Handler Backward Inclined Backplated Radial Blade Belt Driven Single Width, Single Inlet Arrangement 10; U=17 5/8"; UNIT_SIZE=290; W=8"; X=42 11/16"; Y=37 5/8"; Z=54 7/8"
- 290_MHR_ARR_10: (B + 1/4") / 2=12 1/4"; (C/2)+2"=16 1/2"; (C/2)-.125"=14 3/8"; (N-A)/2=9 9/32"; -((B + 1/4") / 2)=-12 1/4"; -D=-46 1/2"; -D+.125"=-46 3/8"; -F=-45 9/16"; -R*.75=-21 9/16"; 2S=29 5/8"; 2T=5 7/8"; 91*AA=32 17/32"; A=27 5/16"; A+.25"=27 9/16"; A/2=13 21/32"; A/5=5 15/32"; AA=35 3/4"; B=24 1/4"; B+.25"=24 1/2"; B/2=12 1/8"; BB=33 7/8"; C=29"; C/2=14 1/2"; D=46 1/2"; E=22 1/2"; E-2"=20 1/2"; E/2=11 1/4"; F=45 9/16"; G=62 3/16"; H=92 1/2"; J=8"; K=21 1/4"; L=39 1/2"; M=31 3/4"; M*.9=26 9/32"; M-(A/5)=26 9/32"; M/2=15 7/8"; Model=MHR; N=45 7/8"; N-A=18 9/16"; P=13/16"; P/2=13/32"; Q=14 3/8"; R=28 3/4"; R*.75=-21 9/16"; S=14 13/16"; SECOND_CURVE=3 13/32"; T=2 15/16"; T+T+1"=6 7/8"; T/2=1 15/32"; THIRD_CURVE=4 9/16"; Type Comments=Industrial Material Handler Backward Inclined Reinforced Radial Blade Belt Driven Single Width, Single Inlet Arrangement 10; U=17 5/8"; UNIT_SIZE=290; W=8"; X=42 11/16"; Y=37 5/8"; Z=54 7/8"
- 70_MHB_ARR_10: (B + 1/4") / 2=3 1/16"; (C/2)+2"=5 1/2"; (C/2)-.125"=3 3/8"; (N-A)/2=1 31/32"; -((B + 1/4") / 2)=-3 1/16"; -D=-14 1/4"; -D+.125"=-14 1/8"; -F=-21 1/16"; -R*.75=-11 5/32"; 2S=8 1/2"; 2T=2 3/8"; 91*AA=8 1/32"; A=6 5/8"; A+.25"=6 7/8"; A/2=3 5/16"; A/5=1 5/16"; AA=8 13/16"; B=5 7/8"; B+.25"=6 1/8"; B/2=2 15/16"; BB=8 3/8"; C=7"; C/2=3 1/2"; D=14 1/4"; E=9 11/16"; E-2"=7 11/16"; E/2=4 27/32"; F=21 1/16"; G=26 1/4"; H=24 3/16"; J=4"; K=9 3/16"; L=9 11/16"; M=8 5/16"; M*.9=7"; M-(A/5)=7"; M/2=4 5/32"; Model=MHB; N=10 9/16"; N-A=3 15/16"; P=9/16"; P/2=9/32"; Q=7 7/16"; R=14 7/8"; R*.75=-11 5/32"; S=4 1/4"; SECOND_CURVE=27/32"; T=1 3/16"; T+T+1"=3 3/8"; T/2=19/32"; THIRD_CURVE=1 3/32"; Type Comments=Industrial Material Handler Backward Inclined Backplated Radial Blade Belt Driven Single Width, Single Inlet Arrangement 10; U=6 3/16"; UNIT_SIZE=70; W=6"; X=10 1/8"; Y=9 1/4"; Z=13 3/8"
- 70_MHR_ARR_10: (B + 1/4") / 2=3 1/16"; (C/2)+2"=5 1/2"; (C/2)-.125"=3 3/8"; (N-A)/2=1 31/32"; -((B + 1/4") / 2)=-3 1/16"; -D=-14 1/4"; -D+.125"=-14 1/8"; -F=-21 1/16"; -R*.75=-11 5/32"; 2S=8 1/2"; 2T=2 3/8"; 91*AA=8 1/32"; A=6 5/8"; A+.25"=6 7/8"; A/2=3 5/16"; A/5=1 5/16"; AA=8 13/16"; B=5 7/8"; B+.25"=6 1/8"; B/2=2 15/16"; BB=8 3/8"; C=7"; C/2=3 1/2"; D=14 1/4"; E=9 11/16"; E-2"=7 11/16"; E/2=4 27/32"; F=21 1/16"; G=26 1/4"; H=24 3/16"; J=4"; K=9 3/16"; L=9 11/16"; M=8 5/16"; M*.9=7"; M-(A/5)=7"; M/2=4 5/32"; Model=MHR; N=10 9/16"; N-A=3 15/16"; P=9/16"; P/2=9/32"; Q=7 7/16"; R=14 7/8"; R*.75=-11 5/32"; S=4 1/4"; SECOND_CURVE=27/32"; T=1 3/16"; T+T+1"=3 3/8"; T/2=19/32"; THIRD_CURVE=1 3/32"; Type Comments=Industrial Material Handler Backward Inclined Reinforced Radial Blade Belt Driven Single Width, Single Inlet Arrangement 10; U=6 3/16"; UNIT_SIZE=70; W=6"; X=10 1/8"; Y=9 1/4"; Z=13 3/8"
- 90_MHB_ARR_10: (B + 1/4") / 2=3 7/8"; (C/2)+2"=6 1/2"; (C/2)-.125"=4 3/8"; (N-A)/2=2 17/32"; -((B + 1/4") / 2)=-3 7/8"; -D=-15 1/4"; -D+.125"=-15 1/8"; -F=-21 7/8"; -R*.75=-11 5/32"; 2S=10 1/8"; 2T=2 7/8"; 91*AA=10 3/16"; A=8 7/16"; A+.25"=8 11/16"; A/2=4 7/32"; A/5=1 11/16"; AA=11 3/16"; B=7 1/2"; B+.25"=7 3/4"; B/2=3 3/4"; BB=10 5/8"; C=9"; C/2=4 1/2"; D=15 1/4"; E=9 11/16"; E-2"=7 11/16"; E/2=4 27/32"; F=21 7/8"; G=27 7/8"; H=28 3/4"; J=4"; K=9 3/16"; L=12 5/16"; M=10 5/8"; M*.9=8 15/16"; M-(A/5)=8 15/16"; M/2=5 5/16"; Model=MHB; N=13 1/2"; N-A=5 1/16"; P=9/16"; P/2=9/32"; Q=7 7/16"; R=14 7/8"; R*.75=-11 5/32"; S=5 1/16"; SECOND_CURVE=1 1/16"; T=1 7/16"; T+T+1"=3 7/8"; T/2=23/32"; THIRD_CURVE=1 13/32"; Type Comments=Industrial Material Handler Backward Inclined Backplated Radial Blade Belt Driven Single Width, Single Inlet Arrangement 10; U=7"; UNIT_SIZE=90; W=6"; X=12 15/16"; Y=11 3/4"; Z=17 1/16"
- 90_MHR_ARR_10: (B + 1/4") / 2=3 7/8"; (C/2)+2"=6 1/2"; (C/2)-.125"=4 3/8"; (N-A)/2=2 17/32"; -((B + 1/4") / 2)=-3 7/8"; -D=-15 1/4"; -D+.125"=-15 1/8"; -F=-21 7/8"; -R*.75=-11 5/32"; 2S=10 1/8"; 2T=2 7/8"; 91*AA=10 3/16"; A=8 7/16"; A+.25"=8 11/16"; A/2=4 7/32"; A/5=1 11/16"; AA=11 3/16"; B=7 1/2"; B+.25"=7 3/4"; B/2=3 3/4"; BB=10 5/8"; C=9"; C/2=4 1/2"; D=15 1/4"; E=9 11/16"; E-2"=7 11/16"; E/2=4 27/32"; F=21 7/8"; G=27 7/8"; H=28 3/4"; J=4"; K=9 3/16"; L=12 5/16"; M=10 5/8"; M*.9=8 15/16"; M-(A/5)=8 15/16"; M/2=5 5/16"; Model=MHR; N=13 1/2"; N-A=5 1/16"; P=9/16"; P/2=9/32"; Q=7 7/16"; R=14 7/8"; R*.75=-11 5/32"; S=5 1/16"; SECOND_CURVE=1 1/16"; T=1 7/16"; T+T+1"=3 7/8"; T/2=23/32"; THIRD_CURVE=1 13/32"; Type Comments=Industrial Material Handler Backward Inclined Reinforced Radial Blade Belt Driven Single Width, Single Inlet Arrangement 10; U=7"; UNIT_SIZE=90; W=6"; X=12 15/16"; Y=11 3/4"; Z=17 1/16"
- 110_MH_ARR_10: (B + 1/4") / 2=4 11/16"; (C/2)+2"=7 1/2"; (C/2)-.125"=5 3/8"; (N-A)/2=3 1/32"; -((B + 1/4") / 2)=-4 11/16"; -D=-18 3/4"; -D+.125"=-18 5/8"; -F=-25"; -R*.75=-12 3/8"; 2S=13"; 2T=2 7/8"; 91*AA=12 1/2"; A=10 3/8"; A+.25"=10 5/8"; A/2=5 3/16"; A/5=2 1/16"; AA=13 3/4"; B=9 1/8"; B+.25"=9 3/8"; B/2=4 9/16"; BB=13 1/16"; C=11"; C/2=5 1/2"; D=18 3/4"; E=9 11/16"; E-2"=7 11/16"; E/2=4 27/32"; F=25"; G=32 7/8"; H=35 3/16"; J=4"; K=9 3/16"; L=15 1/16"; M=13"; M*.9=10 15/16"; M-(A/5)=10 15/16"; M/2=6 1/2"; Model=MH; N=16 7/16"; N-A=6 1/16"; P=9/16"; P/2=9/32"; Q=8 1/4"; R=16 1/2"; R*.75=-12 3/8"; S=6 1/2"; SECOND_CURVE=1 5/16"; T=1 7/16"; T+T+1"=3 7/8"; T/2=23/32"; THIRD_CURVE=1 23/32"; Type Comments=Industrial Material Handler Backward Inclined Radial Blade Belt Driven Single Width, Single Inlet Arrangement 10; U=8 13/16"; UNIT_SIZE=110; W=8"; X=15 3/4"; Y=14 7/16"; Z=20 13/16"
- 130_MH_ARR_10: (B + 1/4") / 2=5 9/16"; (C/2)+2"=8 1/2"; (C/2)-.125"=6 3/8"; (N-A)/2=3 5/8"; -((B + 1/4") / 2)=-5 9/16"; -D=-21 3/4"; -D+.125"=-21 5/8"; -F=-26 3/16"; -R*.75=-12 9/16"; 2S=14 3/4"; 2T=3 3/8"; 91*AA=14 23/32"; A=12 3/16"; A+.25"=12 7/16"; A/2=6 3/32"; A/5=2 7/16"; AA=16 3/16"; B=10 7/8"; B+.25"=11 1/8"; B/2=5 7/16"; BB=15 3/8"; C=13"; C/2=6 1/2"; D=21 3/4"; E=11 3/4"; E-2"=9 3/4"; E/2=5 7/8"; F=26 3/16"; G=34 7/8"; H=41 3/16"; J=5"; K=11"; L=17 13/16"; M=15 3/8"; M*.9=12 15/16"; M-(A/5)=12 15/16"; M/2=7 11/16"; Model=MH; N=19 7/16"; N-A=7 1/4"; P=11/16"; P/2=11/32"; Q=8 3/8"; R=16 3/4"; R*.75=-12 9/16"; S=7 3/8"; SECOND_CURVE=1 17/32"; T=1 11/16"; T+T+1"=4 3/8"; T/2=27/32"; THIRD_CURVE=2 1/32"; Type Comments=Industrial Material Handler Backward Inclined Radial Blade Belt Driven Single Width, Single Inlet Arrangement 10; U=9 13/16"; UNIT_SIZE=130; W=8"; X=18 5/8"; Y=17"; Z=24 5/8"
- 150_MH_ARR_10: (B + 1/4") / 2=6 13/32"; (C/2)+2"=9 1/2"; (C/2)-.125"=7 3/8"; (N-A)/2=4 5/32"; -((B + 1/4") / 2)=-6 13/32"; -D=-25 1/4"; -D+.125"=-25 1/8"; -F=-31 3/4"; -R*.75=-16 1/8"; 2S=16 7/16"; 2T=3 7/8"; 91*AA=17 3/16"; A=14 1/16"; A+.25"=14 5/16"; A/2=7 1/32"; A/5=2 13/16"; AA=18 7/8"; B=12 9/16"; B+.25"=12 13/16"; B/2=6 9/32"; BB=18"; C=15"; C/2=7 1/2"; D=25 1/4"; E=13"; E-2"=11"; E/2=6 1/2"; F=31 3/4"; G=41 5/16"; H=47 5/8"; J=5"; K=12 1/4"; L=20 5/8"; M=17 3/4"; M*.9=14 15/16"; M-(A/5)=14 15/16"; M/2=8 7/8"; Model=MH; N=22 3/8"; N-A=8 5/16"; P=11/16"; P/2=11/32"; Q=10 3/4"; R=21 1/2"; R*.75=-16 1/8"; S=8 7/32"; SECOND_CURVE=1 3/4"; T=1 15/16"; T+T+1"=4 7/8"; T/2=31/32"; THIRD_CURVE=2 11/32"; Type Comments=Industrial Material Handler Backward Inclined Radial Blade Belt Driven Single Width, Single Inlet Arrangement 10; U=10 11/16"; UNIT_SIZE=150; W=8"; X=21 1/2"; Y=19 3/4"; Z=28 3/8"
- 170_MH_ARR_10: (B + 1/4") / 2=7 1/4"; (C/2)+2"=10 1/2"; (C/2)-.125"=8 3/8"; (N-A)/2=4 11/16"; -((B + 1/4") / 2)=-7 1/4"; -D=-28 1/4"; -D+.125"=-28 1/8"; -F=-32 9/16"; -R*.75=-16 1/8"; 2S=18 1/8"; 2T=4 3/8"; 91*AA=19 11/32"; A=16"; A+.25"=16 1/4"; A/2=8"; A/5=3 3/16"; AA=21 1/4"; B=14 1/4"; B+.25"=14 1/2"; B/2=7 1/8"; BB=20 1/4"; C=17"; C/2=8 1/2"; D=28 1/4"; E=13 7/8"; E-2"=11 7/8"; E/2=6 15/16"; F=32 9/16"; G=43"; H=53 5/8"; J=6"; K=13 1/8"; L=23 3/4"; M=20 1/8"; M*.9=16 15/16"; M-(A/5)=16 15/16"; M/2=10 1/16"; Model=MH; N=25 3/8"; N-A=9 3/8"; P=11/16"; P/2=11/32"; Q=10 3/4"; R=21 1/2"; R*.75=-16 1/8"; S=9 1/16"; SECOND_CURVE=2"; T=2 3/16"; T+T+1"=5 3/8"; T/2=1 3/32"; THIRD_CURVE=2 21/32"; Type Comments=Industrial Material Handler Backward Inclined Radial Blade Belt Driven Single Width, Single Inlet Arrangement 10; U=11 1/2"; UNIT_SIZE=170; W=8"; X=24 9/16"; Y=22 1/2"; Z=32 3/16"
- 190_MH_ARR_10: (B + 1/4") / 2=8 1/16"; (C/2)+2"=11 1/2"; (C/2)-.125"=9 3/8"; (N-A)/2=5 7/32"; -((B + 1/4") / 2)=-8 1/16"; -D=-31 1/4"; -D+.125"=-31 1/8"; -F=-34 11/16"; -R*.75=-17 1/16"; 2S=19 7/8"; 2T=4 7/8"; 91*AA=21 5/8"; A=17 13/16"; A+.25"=18 1/16"; A/2=8 29/32"; A/5=3 9/16"; AA=23 3/4"; B=15 7/8"; B+.25"=16 1/8"; B/2=7 15/16"; BB=22 5/8"; C=19"; C/2=9 1/2"; D=31 1/4"; E=15 5/16"; E-2"=13 5/16"; E/2=7 21/32"; F=34 11/16"; G=46"; H=59 1/2"; J=6"; K=14 9/16"; L=25 15/16"; M=22 7/16"; M*.9=18 7/8"; M-(A/5)=18 7/8"; M/2=11 7/32"; Model=MH; N=28 1/4"; N-A=10 7/16"; P=11/16"; P/2=11/32"; Q=11 3/8"; R=22 3/4"; R*.75=-17 1/16"; S=9 15/16"; SECOND_CURVE=2 7/32"; T=2 7/16"; T+T+1"=5 7/8"; T/2=1 7/32"; THIRD_CURVE=2 31/32"; Type Comments=Industrial Material Handler Backward Inclined Radial Blade Belt Driven Single Width, Single Inlet Arrangement 10; U=12 5/16"; UNIT_SIZE=190; W=8"; X=27 1/8"; Y=24 7/8"; Z=35 13/16"
- 210_MH_ARR_10: (B + 1/4") / 2=8 29/32"; (C/2)+2"=12 1/2"; (C/2)-.125"=10 3/8"; (N-A)/2=5 3/4"; -((B + 1/4") / 2)=-8 29/32"; -D=-34 1/2"; -D+.125"=-34 3/8"; -F=-38 1/4"; -R*.75=-19 1/8"; 2S=21 5/16"; 2T=4 7/8"; 91*AA=23 7/16"; A=19 3/4"; A+.25"=20"; A/2=9 7/8"; A/5=3 15/16"; AA=25 3/4"; B=17 9/16"; B+.25"=17 13/16"; B/2=8 25/32"; BB=24 3/8"; C=21"; C/2=10 1/2"; D=34 1/2"; E=16 9/16"; E-2"=14 9/16"; E/2=8 9/32"; F=38 1/4"; G=50 3/8"; H=65 3/4"; J=6"; K=15 13/16"; L=28 1/2"; M=23"; M*.9=19 1/16"; M-(A/5)=19 1/16"; M/2=11 1/2"; Model=MH; N=31 1/4"; N-A=11 1/2"; P=11/16"; P/2=11/32"; Q=12 3/4"; R=25 1/2"; R*.75=-19 1/8"; S=10 21/32"; SECOND_CURVE=2 15/32"; T=2 7/16"; T+T+1"=5 7/8"; T/2=1 7/32"; THIRD_CURVE=3 9/32"; Type Comments=Industrial Material Handler Backward Inclined Radial Blade Belt Driven Single Width, Single Inlet Arrangement 10; U=13 3/16"; UNIT_SIZE=210; W=8"; X=29 7/8"; Y=27 1/8"; Z=38 3/8"
- 230_MH_ARR_10: (B + 1/4") / 2=9 3/4"; (C/2)+2"=13 1/2"; (C/2)-.125"=11 3/8"; (N-A)/2=6 11/32"; -((B + 1/4") / 2)=-9 3/4"; -D=-37 1/2"; -D+.125"=-37 3/8"; -F=-41 1/8"; -R*.75=-20 5/32"; 2S=24 5/8"; 2T=5 3/8"; 91*AA=25 3/4"; A=21 5/8"; A+.25"=21 7/8"; A/2=10 13/16"; A/5=4 5/16"; AA=28 5/16"; B=19 1/4"; B+.25"=19 1/2"; B/2=9 5/8"; BB=26 13/16"; C=23"; C/2=11 1/2"; D=37 1/2"; E=18 13/16"; E-2"=16 13/16"; E/2=9 13/32"; F=41 1/8"; G=55 1/4"; H=71 13/16"; J=7"; K=17 9/16"; L=31 1/4"; M=26"; M*.9=21 11/16"; M-(A/5)=21 11/16"; M/2=13"; Model=MH; N=34 5/16"; N-A=12 11/16"; P=13/16"; P/2=13/32"; Q=13 7/16"; R=26 7/8"; R*.75=-20 5/32"; S=12 5/16"; SECOND_CURVE=2 23/32"; T=2 11/16"; T+T+1"=6 3/8"; T/2=1 11/32"; THIRD_CURVE=3 19/32"; Type Comments=Industrial Material Handler Backward Inclined Radial Blade Belt Driven Single Width, Single Inlet Arrangement 10; U=15 1/8"; UNIT_SIZE=230; W=8"; X=32 13/16"; Y=29 13/16"; Z=42 5/8"
- 260_MH_ARR_10: (B + 1/4") / 2=11"; (C/2)+2"=15"; (C/2)-.125"=12 7/8"; (N-A)/2=8 3/8"; -((B + 1/4") / 2)=-11"; -D=-41 3/4"; -D+.125"=-41 5/8"; -F=-43 15/16"; -R*.75=-20 13/16"; 2S=27 1/8"; 2T=5 3/8"; 91*AA=29"; A=24 7/16"; A+.25"=24 11/16"; A/2=12 7/32"; A/5=4 7/8"; AA=31 7/8"; B=21 3/4"; B+.25"=22"; B/2=10 7/8"; BB=30 1/4"; C=26"; C/2=13"; D=41 3/4"; E=20 5/8"; E-2"=18 5/8"; E/2=10 5/16"; F=43 15/16"; G=58 11/16"; H=82 15/16"; J=7"; K=19 3/8"; L=35 1/8"; M=29"; M*.9=24 1/8"; M-(A/5)=24 1/8"; M/2=14 1/2"; Model=MH; N=41 3/16"; N-A=16 3/4"; P=13/16"; P/2=13/32"; Q=13 7/8"; R=27 3/4"; R*.75=-20 13/16"; S=13 9/16"; SECOND_CURVE=3 1/16"; T=2 11/16"; T+T+1"=6 3/8"; T/2=1 11/32"; THIRD_CURVE=4 1/16"; Type Comments=Industrial Material Handler Backward Inclined Radial Blade Belt Driven Single Width, Single Inlet Arrangement 10; U=16 3/8"; UNIT_SIZE=260; W=8"; X=38 3/16"; Y=33 1/2"; Z=49 5/8"
- 290_MH_ARR_10: (B + 1/4") / 2=12 1/4"; (C/2)+2"=16 1/2"; (C/2)-.125"=14 3/8"; (N-A)/2=9 9/32"; -((B + 1/4") / 2)=-12 1/4"; -D=-46 1/2"; -D+.125"=-46 3/8"; -F=-45 9/16"; -R*.75=-21 9/16"; 2S=29 5/8"; 2T=5 7/8"; 91*AA=32 17/32"; A=27 5/16"; A+.25"=27 9/16"; A/2=13 21/32"; A/5=5 15/32"; AA=35 3/4"; B=24 1/4"; B+.25"=24 1/2"; B/2=12 1/8"; BB=33 7/8"; C=29"; C/2=14 1/2"; D=46 1/2"; E=22 1/2"; E-2"=20 1/2"; E/2=11 1/4"; F=45 9/16"; G=62 3/16"; H=92 1/2"; J=8"; K=21 1/4"; L=39 1/2"; M=31 3/4"; M*.9=26 9/32"; M-(A/5)=26 9/32"; M/2=15 7/8"; Model=MH; N=45 7/8"; N-A=18 9/16"; P=13/16"; P/2=13/32"; Q=14 3/8"; R=28 3/4"; R*.75=-21 9/16"; S=14 13/16"; SECOND_CURVE=3 13/32"; T=2 15/16"; T+T+1"=6 7/8"; T/2=1 15/32"; THIRD_CURVE=4 9/16"; Type Comments=Industrial Material Handler Backward Inclined Radial Blade Belt Driven Single Width, Single Inlet Arrangement 10; U=17 5/8"; UNIT_SIZE=290; W=8"; X=42 11/16"; Y=37 5/8"; Z=54 7/8"
- 70_MH_ARR_10: (B + 1/4") / 2=3 1/16"; (C/2)+2"=5 1/2"; (C/2)-.125"=3 3/8"; (N-A)/2=1 31/32"; -((B + 1/4") / 2)=-3 1/16"; -D=-14 1/4"; -D+.125"=-14 1/8"; -F=-21 1/16"; -R*.75=-11 5/32"; 2S=8 1/2"; 2T=2 3/8"; 91*AA=8 1/32"; A=6 5/8"; A+.25"=6 7/8"; A/2=3 5/16"; A/5=1 5/16"; AA=8 13/16"; B=5 7/8"; B+.25"=6 1/8"; B/2=2 15/16"; BB=8 3/8"; C=7"; C/2=3 1/2"; D=14 1/4"; E=9 11/16"; E-2"=7 11/16"; E/2=4 27/32"; F=21 1/16"; G=26 1/4"; H=24 3/16"; J=4"; K=9 3/16"; L=9 11/16"; M=8 5/16"; M*.9=7"; M-(A/5)=7"; M/2=4 5/32"; Model=MH; N=10 9/16"; N-A=3 15/16"; P=9/16"; P/2=9/32"; Q=7 7/16"; R=14 7/8"; R*.75=-11 5/32"; S=4 1/4"; SECOND_CURVE=27/32"; T=1 3/16"; T+T+1"=3 3/8"; T/2=19/32"; THIRD_CURVE=1 3/32"; Type Comments=Industrial Material Handler Backward Inclined Radial Blade Belt Driven Single Width, Single Inlet Arrangement 10; U=6 3/16"; UNIT_SIZE=70; W=6"; X=10 1/8"; Y=9 1/4"; Z=13 3/8"
- 90_MH_ARR_10: (B + 1/4") / 2=3 7/8"; (C/2)+2"=6 1/2"; (C/2)-.125"=4 3/8"; (N-A)/2=2 17/32"; -((B + 1/4") / 2)=-3 7/8"; -D=-15 1/4"; -D+.125"=-15 1/8"; -F=-21 7/8"; -R*.75=-11 5/32"; 2S=10 1/8"; 2T=2 7/8"; 91*AA=10 3/16"; A=8 7/16"; A+.25"=8 11/16"; A/2=4 7/32"; A/5=1 11/16"; AA=11 3/16"; B=7 1/2"; B+.25"=7 3/4"; B/2=3 3/4"; BB=10 5/8"; C=9"; C/2=4 1/2"; D=15 1/4"; E=9 11/16"; E-2"=7 11/16"; E/2=4 27/32"; F=21 7/8"; G=27 7/8"; H=28 3/4"; J=4"; K=9 3/16"; L=12 5/16"; M=10 5/8"; M*.9=8 15/16"; M-(A/5)=8 15/16"; M/2=5 5/16"; Model=MH; N=13 1/2"; N-A=5 1/16"; P=9/16"; P/2=9/32"; Q=7 7/16"; R=14 7/8"; R*.75=-11 5/32"; S=5 1/16"; SECOND_CURVE=1 1/16"; T=1 7/16"; T+T+1"=3 7/8"; T/2=23/32"; THIRD_CURVE=1 13/32"; Type Comments=Industrial Material Handler Backward Inclined Radial Blade Belt Driven Single Width, Single Inlet Arrangement 10; U=7"; UNIT_SIZE=90; W=6"; X=12 15/16"; Y=11 3/4"; Z=17 1/16"

## geometry (parser evidence)
native form markers: Sweep x6
no freeform markers — native parametric forms only
